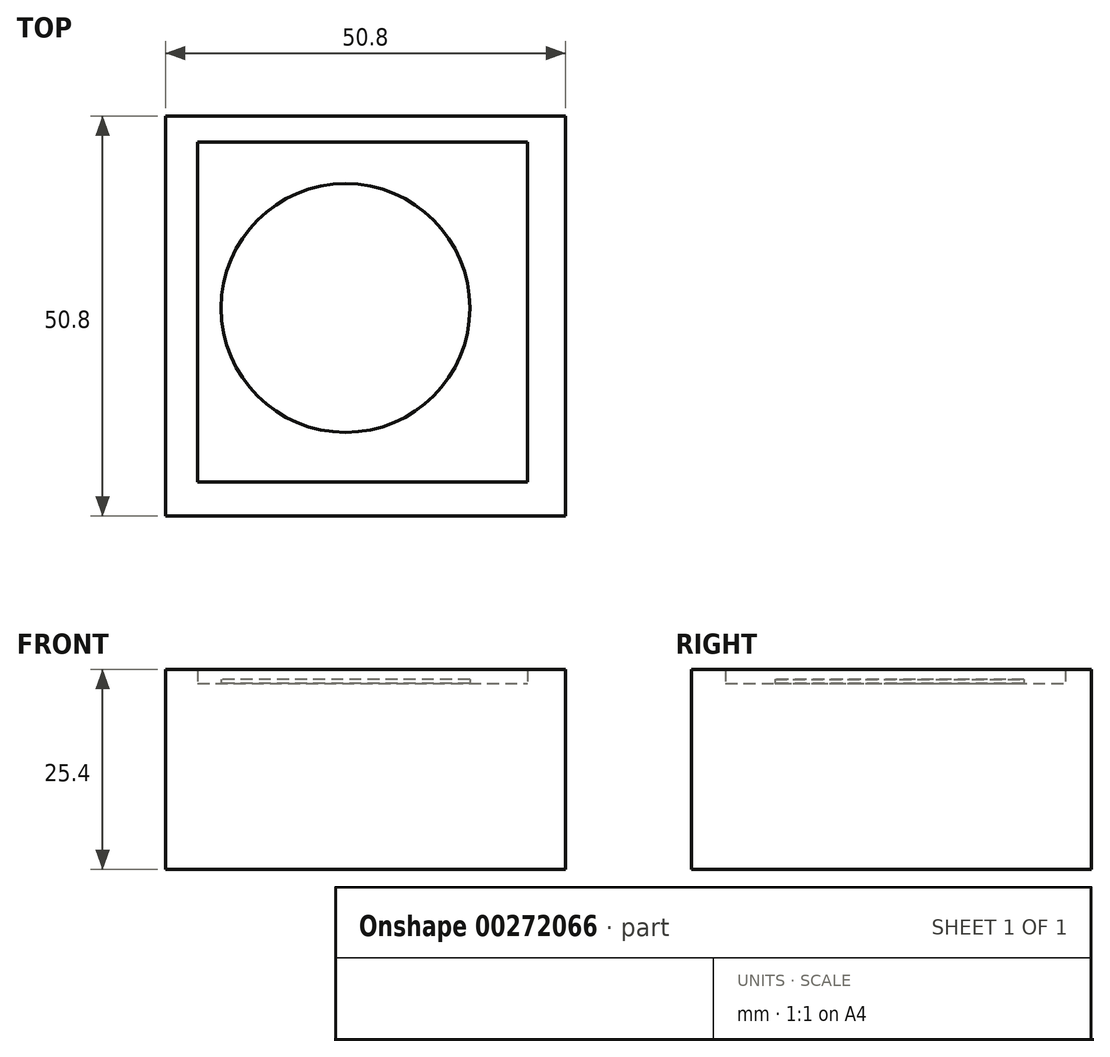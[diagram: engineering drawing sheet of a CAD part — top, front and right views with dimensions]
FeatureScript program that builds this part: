
annotation { "Feature Type Name" : "Feature", "Feature Type Description" : "" }
export const myFeature = defineFeature(function(context is Context, id is Id, definition is map)
    precondition{}
    {
        {
            var Q0;
            Q0=qCreatedBy(makeId("Top.planeOp"),FACE);
            var sketch = newSketch(context, id + "F0", { "sketchPlane" : qUnion([Q0])});
            skLineSegment(sketch, "E0.bottom", {"start": v(-45.97, -18.8) * mm, "end": v(4.83, -18.8) * mm});
            skLineSegment(sketch, "E0.top", {"start": v(-45.97, 32) * mm, "end": v(4.83, 32) * mm});
            skLineSegment(sketch, "E0.left", {"start": v(-45.97, -18.8) * mm, "end": v(-45.97, 32) * mm});
            skLineSegment(sketch, "E0.right", {"start": v(4.83, -18.8) * mm, "end": v(4.83, 32) * mm});
            skCircle(sketch, "E1", {"center": v(-23.11, 7.62) * mm, "radius": 15.8 * mm});
            skLineSegment(sketch, "E2.bottom", {"start": v(-41.91, -14.48) * mm, "end": v(0, -14.48) * mm});
            skLineSegment(sketch, "E2.top", {"start": v(-41.91, 28.7) * mm, "end": v(0, 28.7) * mm});
            skLineSegment(sketch, "E2.left", {"start": v(-41.91, -14.48) * mm, "end": v(-41.91, 28.7) * mm});
            skLineSegment(sketch, "E2.right", {"start": v(0, -14.48) * mm, "end": v(0, 28.7) * mm});
            skSolve(sketch);
        }
        {
            var Q0;
            Q0=makeQuery(id+"F0.imprint","IMPRINT",FACE,{"disambiguationData":[TD([[makeQuery(id+"F0.imprint","IMPRINT",EDGE,{"derivedFrom":sQuery(id+"F0.wireOp",EDGE,"E0.bottom")}),1.0]])]});
            extrude(context, id + "F1", {"entities" : qUnion([Q0]), "depth" : 25.4 * mm});
        }
        {
            var Q0;
            Q0 = qSketchRegion(id + "F0", true);
            var Q1;
            Q1=makeQuery(id+"F0.imprint","IMPRINT",FACE,{"disambiguationData":[TD([[makeQuery(id+"F0.imprint","IMPRINT",EDGE,{"derivedFrom":sQuery(id+"F0.wireOp",EDGE,"E1")}),-1.0]])]});
            extrude(context, id + "F2", {"entities" : qUnion([Q0, Q1]), "operationType" : NewBodyOperationType.ADD, "depth" : 23.62 * mm});
        }
        {
            var Q0;
            Q0=makeQuery(id+"F0.imprint","IMPRINT",FACE,{"disambiguationData":[TD([[makeQuery(id+"F0.imprint","IMPRINT",EDGE,{"derivedFrom":sQuery(id+"F0.wireOp",EDGE,"E1")}),1.0]])]});
            extrude(context, id + "F3", {"entities" : qUnion([Q0]), "operationType" : NewBodyOperationType.ADD, "depth" : 24.13 * mm});
        }
    });
